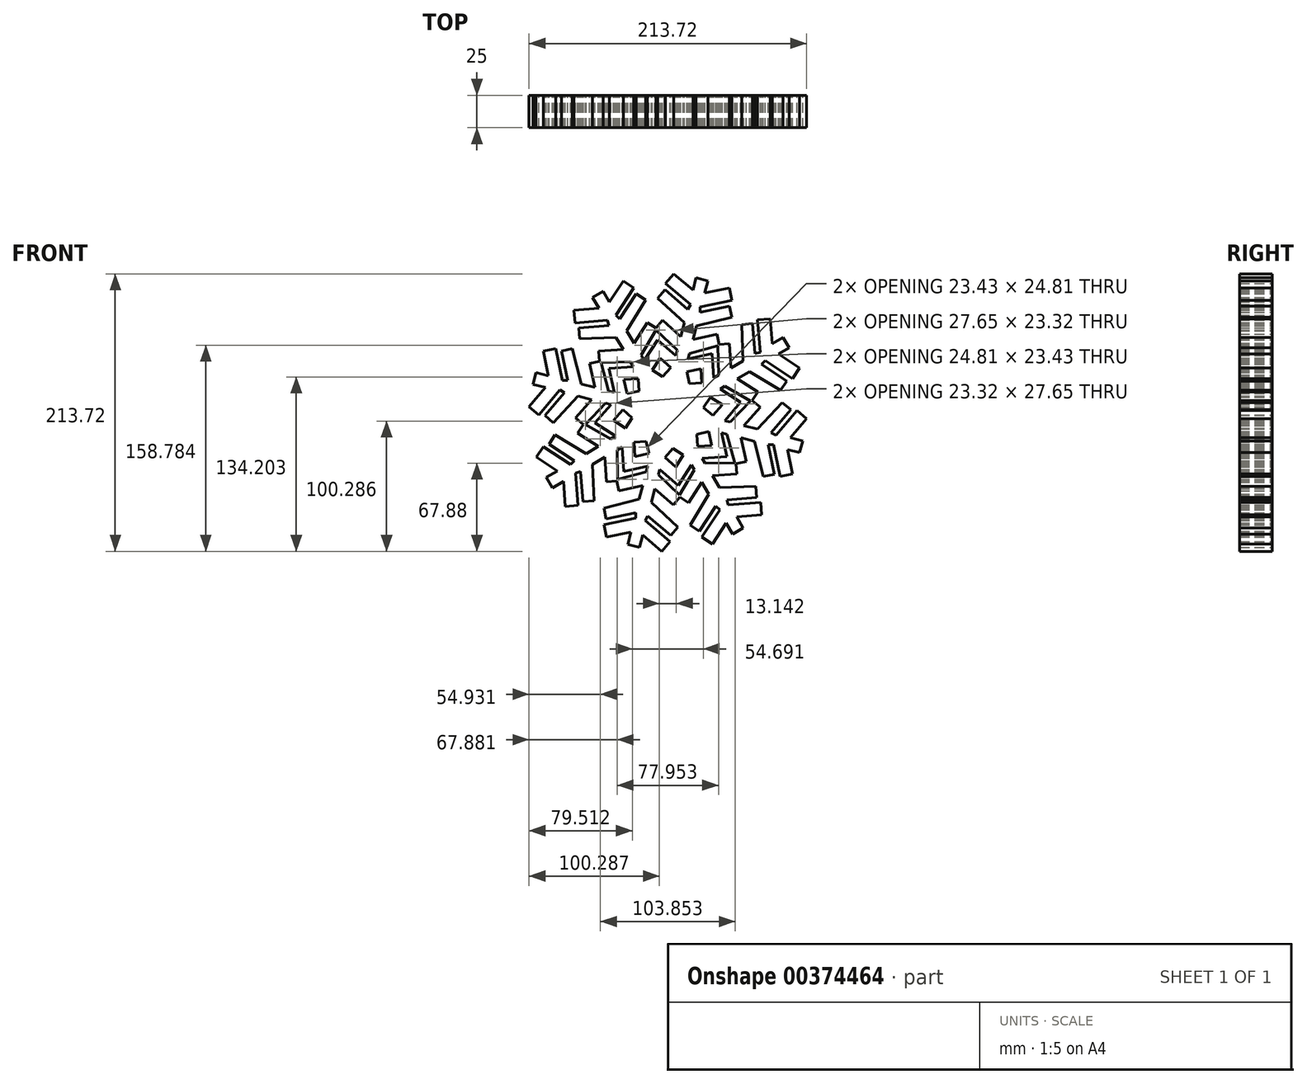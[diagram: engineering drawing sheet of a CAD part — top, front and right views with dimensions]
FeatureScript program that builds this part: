
annotation { "Feature Type Name" : "Feature", "Feature Type Description" : "" }
export const myFeature = defineFeature(function(context is Context, id is Id, definition is map)
    precondition{}
    {
        {
            var Q0;
            Q0=qCreatedBy(makeId("Front.planeOp"),FACE);
            var sketch = newSketch(context, id + "F0", { "sketchPlane" : qUnion([Q0])});
            skPoint(sketch, "E0.first.point", {"position": v(-46.74, 41.12) * mm});
            skPoint(sketch, "E0.second.point", {"position": v(0, 29.5) * mm});
            skPoint(sketch, "E0.third.point", {"position": v(-21.47, 0) * mm});
            skLineSegment(sketch, "E1", {"start": v(5.05, 127.1) * mm, "end": v(2.64, 117.71) * mm});
            skLineSegment(sketch, "E2", {"start": v(2.64, 117.71) * mm, "end": v(21.57, 121.6) * mm});
            skLineSegment(sketch, "E3", {"start": v(21.57, 121.6) * mm, "end": v(23.54, 112.02) * mm});
            skLineSegment(sketch, "E4", {"start": v(23.54, 112.02) * mm, "end": v(-1, 106.97) * mm});
            skLineSegment(sketch, "E5", {"start": v(-1, 106.97) * mm, "end": v(-1, 102.86) * mm});
            skLineSegment(sketch, "E6", {"start": v(-1, 102.86) * mm, "end": v(21.7, 107.53) * mm});
            skLineSegment(sketch, "E7", {"start": v(21.7, 107.53) * mm, "end": v(23.41, 99.23) * mm});
            skLineSegment(sketch, "E8", {"start": v(23.41, 99.23) * mm, "end": v(-3.7, 92.41) * mm});
            skLineSegment(sketch, "E9", {"start": v(-3.7, 92.41) * mm, "end": v(-6.38, 81.93) * mm});
            skLineSegment(sketch, "E10", {"start": v(-6.38, 81.93) * mm, "end": v(12.02, 86) * mm});
            skLineSegment(sketch, "E11", {"start": v(12.02, 86) * mm, "end": v(13.63, 78.2) * mm});
            skLineSegment(sketch, "E12", {"start": v(13.8, 77.34) * mm, "end": v(-9.05, 71.25) * mm});
            skLineSegment(sketch, "E13", {"start": v(-9.05, 71.25) * mm, "end": v(-10.13, 67) * mm});
            skLineSegment(sketch, "E14", {"start": v(-10.13, 67) * mm, "end": v(8.24, 71.01) * mm});
            skLineSegment(sketch, "E15", {"start": v(-0.39, 59.51) * mm, "end": v(-11.08, 57.14) * mm});
            skLineSegment(sketch, "E16", {"start": v(-11.08, 57.14) * mm, "end": v(-9.05, 47.8) * mm});
            skLineSegment(sketch, "E17", {"start": v(0.52, 128.27) * mm, "end": v(5.05, 127.1) * mm});
            skPoint(sketch, "E18.orphan", {"position": v(0, 107.18) * mm});
            skLineSegment(sketch, "E19.MirrorCS", {"start": v(-23.5, 60.32) * mm, "end": v(-29.78, 53.12) * mm});
            skLineSegment(sketch, "E20.MirrorCS", {"start": v(-31.74, 67.55) * mm, "end": v(-23.5, 60.32) * mm});
            skLineSegment(sketch, "E21.MirrorCS", {"start": v(-19.6, 69.43) * mm, "end": v(-33.77, 81.78) * mm});
            skLineSegment(sketch, "E22.MirrorCS", {"start": v(-18.5, 73.67) * mm, "end": v(-19.6, 69.43) * mm});
            skLineSegment(sketch, "E23.MirrorCS", {"start": v(-35.6, 90) * mm, "end": v(-18.5, 73.67) * mm});
            skLineSegment(sketch, "E24.MirrorCS", {"start": v(-29.88, 96.74) * mm, "end": v(-35.04, 90.67) * mm});
            skLineSegment(sketch, "E25.MirrorCS", {"start": v(-15.7, 84.32) * mm, "end": v(-29.88, 96.74) * mm});
            skLineSegment(sketch, "E26.MirrorCS", {"start": v(-13.02, 94.8) * mm, "end": v(-15.7, 84.32) * mm});
            skLineSegment(sketch, "E27.MirrorCS", {"start": v(-33.5, 113.82) * mm, "end": v(-13.02, 94.8) * mm});
            skLineSegment(sketch, "E28.MirrorCS", {"start": v(-28.02, 120.27) * mm, "end": v(-33.5, 113.82) * mm});
            skLineSegment(sketch, "E29.MirrorCS", {"start": v(-10.37, 105.26) * mm, "end": v(-28.02, 120.27) * mm});
            skLineSegment(sketch, "E30.MirrorCS", {"start": v(-8.39, 108.87) * mm, "end": v(-10.37, 105.26) * mm});
            skLineSegment(sketch, "E31.MirrorCS", {"start": v(-27.47, 125.1) * mm, "end": v(-8.39, 108.87) * mm});
            skLineSegment(sketch, "E32.MirrorCS", {"start": v(-21.13, 132.55) * mm, "end": v(-27.47, 125.1) * mm});
            skLineSegment(sketch, "E33.MirrorCS", {"start": v(-6.41, 120.03) * mm, "end": v(-21.13, 132.55) * mm});
            skLineSegment(sketch, "E34.MirrorCS", {"start": v(0.52, 128.27) * mm, "end": v(-4, 129.43) * mm});
            skLineSegment(sketch, "E35.MirrorCS", {"start": v(-4, 129.43) * mm, "end": v(-6.41, 120.03) * mm});
            skLineSegment(sketch, "E36.1.0", {"start": v(-52.33, 60.98) * mm, "end": v(-71.09, 59.69) * mm});
            skPoint(sketch, "E36.1.1", {"position": v(-65.17, 101.53) * mm});
            skLineSegment(sketch, "E36.1.2", {"start": v(-71.14, 92.84) * mm, "end": v(-94.24, 90.97) * mm});
            skLineSegment(sketch, "E36.1.3", {"start": v(-34.31, 90.2) * mm, "end": v(-46.16, 69.73) * mm});
            skPoint(sketch, "E36.1.4", {"position": v(-4.56, 10.56) * mm});
            skPoint(sketch, "E36.1.5", {"position": v(-10.24, 46.6) * mm});
            skLineSegment(sketch, "E36.1.6", {"start": v(-62.82, 97.77) * mm, "end": v(-50.07, 117.12) * mm});
            skLineSegment(sketch, "E36.1.7", {"start": v(-51.95, 121.6) * mm, "end": v(-65.73, 100.68) * mm});
            skLineSegment(sketch, "E36.1.10", {"start": v(-51.82, 79.16) * mm, "end": v(-41.7, 95.06) * mm});
            skLineSegment(sketch, "E36.1.11", {"start": v(-43, 112.46) * mm, "end": v(-57.34, 88.47) * mm});
            skLineSegment(sketch, "E36.1.12", {"start": v(-93.56, 82.53) * mm, "end": v(-65.63, 83.57) * mm});
            skPoint(sketch, "E36.1.13", {"position": v(-51.5, 21.76) * mm});
            skLineSegment(sketch, "E36.1.14", {"start": v(-78.8, 106.08) * mm, "end": v(-98.05, 104.53) * mm});
            skLineSegment(sketch, "E36.1.15", {"start": v(-60.11, 74.25) * mm, "end": v(-78.92, 73.02) * mm});
            skLineSegment(sketch, "E36.1.16", {"start": v(-77.15, 64.23) * mm, "end": v(-54.56, 64.75) * mm});
            skLineSegment(sketch, "E36.1.17", {"start": v(-97.26, 94.77) * mm, "end": v(-72.3, 96.8) * mm});
            skLineSegment(sketch, "E36.1.18", {"start": v(-43.93, 65.95) * mm, "end": v(-33.77, 81.78) * mm});
            skLineSegment(sketch, "E36.1.19", {"start": v(-59.59, 51.06) * mm, "end": v(-48.66, 51.77) * mm});
            skLineSegment(sketch, "E36.1.20", {"start": v(-48.66, 51.77) * mm, "end": v(-48, 42.24) * mm});
            skLineSegment(sketch, "E36.1.21", {"start": v(-70.75, 110.84) * mm, "end": v(-60.12, 126.98) * mm});
            skLineSegment(sketch, "E36.1.22", {"start": v(-37.62, 58.3) * mm, "end": v(-29.58, 53.14) * mm});
            skLineSegment(sketch, "E36.1.23", {"start": v(-31.74, 67.55) * mm, "end": v(-37.62, 58.3) * mm});
            skLineSegment(sketch, "E36.1.24", {"start": v(-72.3, 96.8) * mm, "end": v(-71.14, 92.84) * mm});
            skLineSegment(sketch, "E36.1.25", {"start": v(-46.16, 69.73) * mm, "end": v(-43.93, 65.95) * mm});
            skLineSegment(sketch, "E36.1.26", {"start": v(-94.24, 90.97) * mm, "end": v(-93.56, 82.53) * mm});
            skLineSegment(sketch, "E36.1.27", {"start": v(-41.7, 95.06) * mm, "end": v(-35.04, 90.67) * mm});
            skLineSegment(sketch, "E36.1.28", {"start": v(-83.73, 114.43) * mm, "end": v(-78.8, 106.08) * mm});
            skLineSegment(sketch, "E36.1.29", {"start": v(-50.07, 117.12) * mm, "end": v(-43, 112.46) * mm});
            skLineSegment(sketch, "E36.1.30", {"start": v(-60.12, 126.98) * mm, "end": v(-51.95, 121.6) * mm});
            skLineSegment(sketch, "E36.1.31", {"start": v(-75.7, 119.19) * mm, "end": v(-70.75, 110.84) * mm});
            skLineSegment(sketch, "E36.1.32", {"start": v(-57.34, 88.47) * mm, "end": v(-51.82, 79.16) * mm});
            skLineSegment(sketch, "E36.1.33", {"start": v(-65.63, 83.57) * mm, "end": v(-60.11, 74.25) * mm});
            skLineSegment(sketch, "E36.1.34", {"start": v(-78.92, 73.02) * mm, "end": v(-78.28, 65.08) * mm});
            skLineSegment(sketch, "E36.1.35", {"start": v(-98.05, 104.53) * mm, "end": v(-97.26, 94.77) * mm});
            skLineSegment(sketch, "E36.1.36", {"start": v(-54.56, 64.75) * mm, "end": v(-52.33, 60.98) * mm});
            skLineSegment(sketch, "E36.1.37", {"start": v(-65.73, 100.68) * mm, "end": v(-62.82, 97.77) * mm});
            skLineSegment(sketch, "E36.1.38", {"start": v(-79.71, 116.8) * mm, "end": v(-83.73, 114.43) * mm});
            skLineSegment(sketch, "E36.1.39", {"start": v(-79.71, 116.8) * mm, "end": v(-75.7, 119.19) * mm});
            skLineSegment(sketch, "E36.2.0", {"start": v(-69.5, 31.85) * mm, "end": v(-81.85, 17.68) * mm});
            skPoint(sketch, "E36.2.1", {"position": v(-107.25, 51.45) * mm});
            skLineSegment(sketch, "E36.2.2", {"start": v(-105.33, 41.08) * mm, "end": v(-120.35, 23.43) * mm});
            skLineSegment(sketch, "E36.2.3", {"start": v(-77.15, 64.23) * mm, "end": v(-71.33, 42.4) * mm});
            skPoint(sketch, "E36.2.4", {"position": v(-0.08, 29.98) * mm});
            skPoint(sketch, "E36.2.5", {"position": v(-29.58, 51.45) * mm});
            skLineSegment(sketch, "E36.2.6", {"start": v(-102.93, 50.45) * mm, "end": v(-107.6, 73.16) * mm});
            skLineSegment(sketch, "E36.2.7", {"start": v(-112.1, 74.99) * mm, "end": v(-107.05, 50.45) * mm});
            skLineSegment(sketch, "E36.2.10", {"start": v(-82, 45.07) * mm, "end": v(-86.08, 63.47) * mm});
            skLineSegment(sketch, "E36.2.11", {"start": v(-99.3, 74.86) * mm, "end": v(-92.49, 47.76) * mm});
            skLineSegment(sketch, "E36.2.12", {"start": v(-113.9, 17.94) * mm, "end": v(-94.88, 38.43) * mm});
            skPoint(sketch, "E36.2.13", {"position": v(-41.2, 4.7) * mm});
            skLineSegment(sketch, "E36.2.14", {"start": v(-120.1, 45.04) * mm, "end": v(-132.62, 30.32) * mm});
            skLineSegment(sketch, "E36.2.15", {"start": v(-84.4, 35.74) * mm, "end": v(-96.82, 21.57) * mm});
            skLineSegment(sketch, "E36.2.16", {"start": v(-90.08, 15.84) * mm, "end": v(-73.75, 32.94) * mm});
            skLineSegment(sketch, "E36.2.17", {"start": v(-125.17, 23.98) * mm, "end": v(-108.94, 43.06) * mm});
            skLineSegment(sketch, "E36.2.18", {"start": v(-67.08, 41.32) * mm, "end": v(-71.09, 59.69) * mm});
            skLineSegment(sketch, "E36.2.19", {"start": v(-67.62, 19.7) * mm, "end": v(-60.4, 27.94) * mm});
            skLineSegment(sketch, "E36.2.20", {"start": v(-60.4, 27.94) * mm, "end": v(-53.2, 21.67) * mm});
            skLineSegment(sketch, "E36.2.21", {"start": v(-117.79, 54.1) * mm, "end": v(-121.68, 73.02) * mm});
            skLineSegment(sketch, "E36.2.22", {"start": v(-57.22, 40.36) * mm, "end": v(-47.88, 42.4) * mm});
            skLineSegment(sketch, "E36.2.23", {"start": v(-59.59, 51.06) * mm, "end": v(-57.22, 40.36) * mm});
            skLineSegment(sketch, "E36.2.24", {"start": v(-108.94, 43.06) * mm, "end": v(-105.33, 41.08) * mm});
            skLineSegment(sketch, "E36.2.25", {"start": v(-71.33, 42.4) * mm, "end": v(-67.08, 41.32) * mm});
            skLineSegment(sketch, "E36.2.26", {"start": v(-120.35, 23.43) * mm, "end": v(-113.9, 17.94) * mm});
            skLineSegment(sketch, "E36.2.27", {"start": v(-86.08, 63.47) * mm, "end": v(-78.28, 65.08) * mm});
            skLineSegment(sketch, "E36.2.28", {"start": v(-129.5, 47.45) * mm, "end": v(-120.1, 45.04) * mm});
            skLineSegment(sketch, "E36.2.29", {"start": v(-107.6, 73.16) * mm, "end": v(-99.3, 74.86) * mm});
            skLineSegment(sketch, "E36.2.30", {"start": v(-121.68, 73.02) * mm, "end": v(-112.1, 74.99) * mm});
            skLineSegment(sketch, "E36.2.31", {"start": v(-127.18, 56.5) * mm, "end": v(-117.79, 54.1) * mm});
            skLineSegment(sketch, "E36.2.32", {"start": v(-92.49, 47.76) * mm, "end": v(-82, 45.07) * mm});
            skLineSegment(sketch, "E36.2.33", {"start": v(-94.88, 38.43) * mm, "end": v(-84.4, 35.74) * mm});
            skLineSegment(sketch, "E36.2.34", {"start": v(-96.82, 21.57) * mm, "end": v(-90.75, 16.4) * mm});
            skLineSegment(sketch, "E36.2.35", {"start": v(-132.62, 30.32) * mm, "end": v(-125.17, 23.98) * mm});
            skLineSegment(sketch, "E36.2.36", {"start": v(-73.75, 32.94) * mm, "end": v(-69.5, 31.85) * mm});
            skLineSegment(sketch, "E36.2.37", {"start": v(-107.05, 50.45) * mm, "end": v(-102.93, 50.45) * mm});
            skLineSegment(sketch, "E36.2.38", {"start": v(-128.34, 51.97) * mm, "end": v(-129.5, 47.45) * mm});
            skLineSegment(sketch, "E36.2.39", {"start": v(-128.34, 51.97) * mm, "end": v(-127.18, 56.5) * mm});
            skLineSegment(sketch, "E36.3.0", {"start": v(-61.05, -0.88) * mm, "end": v(-59.76, -19.64) * mm});
            skPoint(sketch, "E36.3.1", {"position": v(-101.6, -13.72) * mm});
            skLineSegment(sketch, "E36.3.2", {"start": v(-92.91, -19.7) * mm, "end": v(-91.04, -42.8) * mm});
            skLineSegment(sketch, "E36.3.3", {"start": v(-90.27, 17.14) * mm, "end": v(-69.8, 5.29) * mm});
            skPoint(sketch, "E36.3.4", {"position": v(-10.64, 46.89) * mm});
            skPoint(sketch, "E36.3.5", {"position": v(-46.68, 41.2) * mm});
            skLineSegment(sketch, "E36.3.6", {"start": v(-97.84, -11.37) * mm, "end": v(-117.2, 1.38) * mm});
            skLineSegment(sketch, "E36.3.7", {"start": v(-121.67, -0.5) * mm, "end": v(-100.75, -14.28) * mm});
            skLineSegment(sketch, "E36.3.10", {"start": v(-79.23, -0.38) * mm, "end": v(-95.13, 9.75) * mm});
            skLineSegment(sketch, "E36.3.11", {"start": v(-112.54, 8.46) * mm, "end": v(-88.55, -5.89) * mm});
            skLineSegment(sketch, "E36.3.12", {"start": v(-82.6, -42.1) * mm, "end": v(-83.64, -14.18) * mm});
            skPoint(sketch, "E36.3.13", {"position": v(-21.84, -0.06) * mm});
            skLineSegment(sketch, "E36.3.14", {"start": v(-106.16, -27.34) * mm, "end": v(-104.6, -46.6) * mm});
            skLineSegment(sketch, "E36.3.15", {"start": v(-74.33, -8.66) * mm, "end": v(-73.1, -27.47) * mm});
            skLineSegment(sketch, "E36.3.16", {"start": v(-64.28, -26.76) * mm, "end": v(-64.83, -3.12) * mm});
            skLineSegment(sketch, "E36.3.17", {"start": v(-94.84, -45.8) * mm, "end": v(-96.87, -20.84) * mm});
            skLineSegment(sketch, "E36.3.18", {"start": v(-66.03, 7.52) * mm, "end": v(-81.85, 17.68) * mm});
            skLineSegment(sketch, "E36.3.19", {"start": v(-51.13, -8.14) * mm, "end": v(-51.85, 2.8) * mm});
            skLineSegment(sketch, "E36.3.20", {"start": v(-51.85, 2.8) * mm, "end": v(-42.31, 3.45) * mm});
            skLineSegment(sketch, "E36.3.21", {"start": v(-110.92, -19.3) * mm, "end": v(-127.05, -8.67) * mm});
            skLineSegment(sketch, "E36.3.22", {"start": v(-58.38, 13.82) * mm, "end": v(-53.22, 21.87) * mm});
            skLineSegment(sketch, "E36.3.23", {"start": v(-67.62, 19.7) * mm, "end": v(-58.38, 13.82) * mm});
            skLineSegment(sketch, "E36.3.24", {"start": v(-96.87, -20.84) * mm, "end": v(-92.91, -19.7) * mm});
            skLineSegment(sketch, "E36.3.25", {"start": v(-69.8, 5.29) * mm, "end": v(-66.03, 7.52) * mm});
            skLineSegment(sketch, "E36.3.26", {"start": v(-91.04, -42.8) * mm, "end": v(-82.6, -42.1) * mm});
            skLineSegment(sketch, "E36.3.27", {"start": v(-95.13, 9.75) * mm, "end": v(-90.75, 16.4) * mm});
            skLineSegment(sketch, "E36.3.28", {"start": v(-114.5, -32.28) * mm, "end": v(-106.16, -27.34) * mm});
            skLineSegment(sketch, "E36.3.29", {"start": v(-117.2, 1.38) * mm, "end": v(-112.54, 8.46) * mm});
            skLineSegment(sketch, "E36.3.30", {"start": v(-127.05, -8.67) * mm, "end": v(-121.67, -0.5) * mm});
            skLineSegment(sketch, "E36.3.31", {"start": v(-119.27, -24.24) * mm, "end": v(-110.92, -19.3) * mm});
            skLineSegment(sketch, "E36.3.32", {"start": v(-88.55, -5.89) * mm, "end": v(-79.23, -0.38) * mm});
            skLineSegment(sketch, "E36.3.33", {"start": v(-83.64, -14.18) * mm, "end": v(-74.33, -8.66) * mm});
            skLineSegment(sketch, "E36.3.34", {"start": v(-73.1, -27.47) * mm, "end": v(-65.15, -26.83) * mm});
            skLineSegment(sketch, "E36.3.35", {"start": v(-104.6, -46.6) * mm, "end": v(-94.84, -45.8) * mm});
            skLineSegment(sketch, "E36.3.36", {"start": v(-64.83, -3.12) * mm, "end": v(-61.05, -0.88) * mm});
            skLineSegment(sketch, "E36.3.37", {"start": v(-100.75, -14.28) * mm, "end": v(-97.84, -11.37) * mm});
            skLineSegment(sketch, "E36.3.38", {"start": v(-116.88, -28.26) * mm, "end": v(-114.5, -32.28) * mm});
            skLineSegment(sketch, "E36.3.39", {"start": v(-116.88, -28.26) * mm, "end": v(-119.27, -24.24) * mm});
            skLineSegment(sketch, "E36.4.0", {"start": v(-31.93, -18.06) * mm, "end": v(-17.75, -30.4) * mm});
            skPoint(sketch, "E36.4.1", {"position": v(-51.52, -55.8) * mm});
            skLineSegment(sketch, "E36.4.2", {"start": v(-41.16, -53.88) * mm, "end": v(-23.5, -68.9) * mm});
            skLineSegment(sketch, "E36.4.3", {"start": v(-65.33, -25.97) * mm, "end": v(-42.48, -19.88) * mm});
            skPoint(sketch, "E36.4.4", {"position": v(-30.06, 51.37) * mm});
            skPoint(sketch, "E36.4.5", {"position": v(-51.52, 21.87) * mm});
            skLineSegment(sketch, "E36.4.6", {"start": v(-50.53, -51.48) * mm, "end": v(-73.23, -56.15) * mm});
            skLineSegment(sketch, "E36.4.7", {"start": v(-75.06, -60.65) * mm, "end": v(-50.53, -55.6) * mm});
            skLineSegment(sketch, "E36.4.10", {"start": v(-45.14, -30.55) * mm, "end": v(-63.54, -34.63) * mm});
            skLineSegment(sketch, "E36.4.11", {"start": v(-74.94, -47.86) * mm, "end": v(-47.83, -41.04) * mm});
            skLineSegment(sketch, "E36.4.12", {"start": v(-18.02, -62.44) * mm, "end": v(-38.5, -43.43) * mm});
            skPoint(sketch, "E36.4.13", {"position": v(-4.78, 10.26) * mm});
            skLineSegment(sketch, "E36.4.14", {"start": v(-45.11, -68.66) * mm, "end": v(-30.4, -81.17) * mm});
            skLineSegment(sketch, "E36.4.15", {"start": v(-35.82, -32.94) * mm, "end": v(-21.65, -45.37) * mm});
            skLineSegment(sketch, "E36.4.16", {"start": v(-15.92, -38.63) * mm, "end": v(-33.02, -22.3) * mm});
            skLineSegment(sketch, "E36.4.17", {"start": v(-24.06, -73.72) * mm, "end": v(-43.14, -57.5) * mm});
            skLineSegment(sketch, "E36.4.18", {"start": v(-41.4, -15.63) * mm, "end": v(-59.76, -19.64) * mm});
            skLineSegment(sketch, "E36.4.19", {"start": v(-19.78, -16.17) * mm, "end": v(-28.02, -8.95) * mm});
            skLineSegment(sketch, "E36.4.20", {"start": v(-28.02, -8.95) * mm, "end": v(-21.74, -1.74) * mm});
            skLineSegment(sketch, "E36.4.21", {"start": v(-54.17, -66.34) * mm, "end": v(-73.1, -70.23) * mm});
            skLineSegment(sketch, "E36.4.22", {"start": v(-40.44, -5.77) * mm, "end": v(-42.48, 3.57) * mm});
            skLineSegment(sketch, "E36.4.23", {"start": v(-51.13, -8.14) * mm, "end": v(-40.44, -5.77) * mm});
            skLineSegment(sketch, "E36.4.24", {"start": v(-43.14, -57.5) * mm, "end": v(-41.16, -53.88) * mm});
            skLineSegment(sketch, "E36.4.25", {"start": v(-42.48, -19.88) * mm, "end": v(-41.4, -15.63) * mm});
            skLineSegment(sketch, "E36.4.26", {"start": v(-23.5, -68.9) * mm, "end": v(-18.02, -62.44) * mm});
            skLineSegment(sketch, "E36.4.27", {"start": v(-63.54, -34.63) * mm, "end": v(-65.15, -26.83) * mm});
            skLineSegment(sketch, "E36.4.28", {"start": v(-47.52, -78.05) * mm, "end": v(-45.11, -68.66) * mm});
            skLineSegment(sketch, "E36.4.29", {"start": v(-73.23, -56.15) * mm, "end": v(-74.94, -47.86) * mm});
            skLineSegment(sketch, "E36.4.30", {"start": v(-73.1, -70.23) * mm, "end": v(-75.06, -60.65) * mm});
            skLineSegment(sketch, "E36.4.31", {"start": v(-56.57, -75.73) * mm, "end": v(-54.17, -66.34) * mm});
            skLineSegment(sketch, "E36.4.32", {"start": v(-47.83, -41.04) * mm, "end": v(-45.14, -30.55) * mm});
            skLineSegment(sketch, "E36.4.33", {"start": v(-38.5, -43.43) * mm, "end": v(-35.82, -32.94) * mm});
            skLineSegment(sketch, "E36.4.34", {"start": v(-21.65, -45.37) * mm, "end": v(-16.48, -39.3) * mm});
            skLineSegment(sketch, "E36.4.35", {"start": v(-30.4, -81.17) * mm, "end": v(-24.06, -73.72) * mm});
            skLineSegment(sketch, "E36.4.36", {"start": v(-33.02, -22.3) * mm, "end": v(-31.93, -18.06) * mm});
            skLineSegment(sketch, "E36.4.37", {"start": v(-50.53, -55.6) * mm, "end": v(-50.53, -51.48) * mm});
            skLineSegment(sketch, "E36.4.38", {"start": v(-52.05, -76.9) * mm, "end": v(-47.52, -78.05) * mm});
            skLineSegment(sketch, "E36.4.39", {"start": v(-52.05, -76.9) * mm, "end": v(-56.57, -75.73) * mm});
            skLineSegment(sketch, "E36.5.0", {"start": v(0.8, -9.6) * mm, "end": v(19.57, -8.31) * mm});
            skPoint(sketch, "E36.5.1", {"position": v(13.64, -50.15) * mm});
            skLineSegment(sketch, "E36.5.2", {"start": v(19.61, -41.47) * mm, "end": v(42.72, -39.6) * mm});
            skLineSegment(sketch, "E36.5.3", {"start": v(-17.21, -38.82) * mm, "end": v(-5.36, -18.35) * mm});
            skPoint(sketch, "E36.5.4", {"position": v(-46.96, 40.81) * mm});
            skPoint(sketch, "E36.5.5", {"position": v(-41.28, 4.77) * mm});
            skLineSegment(sketch, "E36.5.6", {"start": v(11.3, -46.4) * mm, "end": v(-1.46, -65.75) * mm});
            skLineSegment(sketch, "E36.5.7", {"start": v(0.42, -70.22) * mm, "end": v(14.2, -49.3) * mm});
            skLineSegment(sketch, "E36.5.10", {"start": v(0.3, -27.78) * mm, "end": v(-9.82, -43.68) * mm});
            skLineSegment(sketch, "E36.5.11", {"start": v(-8.53, -61.09) * mm, "end": v(5.81, -37.1) * mm});
            skLineSegment(sketch, "E36.5.12", {"start": v(42.03, -31.15) * mm, "end": v(14.1, -32.2) * mm});
            skPoint(sketch, "E36.5.13", {"position": v(-0.02, 29.61) * mm});
            skLineSegment(sketch, "E36.5.14", {"start": v(27.27, -54.71) * mm, "end": v(46.52, -53.15) * mm});
            skLineSegment(sketch, "E36.5.15", {"start": v(8.59, -22.88) * mm, "end": v(27.4, -21.65) * mm});
            skLineSegment(sketch, "E36.5.16", {"start": v(26.68, -12.83) * mm, "end": v(3.04, -13.38) * mm});
            skLineSegment(sketch, "E36.5.17", {"start": v(45.73, -43.4) * mm, "end": v(20.77, -45.42) * mm});
            skLineSegment(sketch, "E36.5.18", {"start": v(-7.6, -14.58) * mm, "end": v(-17.75, -30.4) * mm});
            skLineSegment(sketch, "E36.5.19", {"start": v(8.06, 0.31) * mm, "end": v(-2.87, -0.4) * mm});
            skLineSegment(sketch, "E36.5.20", {"start": v(-2.87, -0.4) * mm, "end": v(-3.52, 9.14) * mm});
            skLineSegment(sketch, "E36.5.21", {"start": v(19.23, -59.47) * mm, "end": v(8.6, -75.6) * mm});
            skLineSegment(sketch, "E36.5.22", {"start": v(-13.9, -6.93) * mm, "end": v(-21.95, -1.77) * mm});
            skLineSegment(sketch, "E36.5.23", {"start": v(-19.78, -16.17) * mm, "end": v(-13.9, -6.93) * mm});
            skLineSegment(sketch, "E36.5.24", {"start": v(20.77, -45.42) * mm, "end": v(19.61, -41.47) * mm});
            skLineSegment(sketch, "E36.5.25", {"start": v(-5.36, -18.35) * mm, "end": v(-7.6, -14.58) * mm});
            skLineSegment(sketch, "E36.5.26", {"start": v(42.72, -39.6) * mm, "end": v(42.03, -31.15) * mm});
            skLineSegment(sketch, "E36.5.27", {"start": v(-9.82, -43.68) * mm, "end": v(-16.48, -39.3) * mm});
            skLineSegment(sketch, "E36.5.28", {"start": v(32.2, -63.06) * mm, "end": v(27.27, -54.71) * mm});
            skLineSegment(sketch, "E36.5.29", {"start": v(-1.46, -65.75) * mm, "end": v(-8.53, -61.09) * mm});
            skLineSegment(sketch, "E36.5.30", {"start": v(8.6, -75.6) * mm, "end": v(0.42, -70.22) * mm});
            skLineSegment(sketch, "E36.5.31", {"start": v(24.17, -67.82) * mm, "end": v(19.23, -59.47) * mm});
            skLineSegment(sketch, "E36.5.32", {"start": v(5.81, -37.1) * mm, "end": v(0.3, -27.78) * mm});
            skLineSegment(sketch, "E36.5.33", {"start": v(14.1, -32.2) * mm, "end": v(8.59, -22.88) * mm});
            skLineSegment(sketch, "E36.5.34", {"start": v(27.4, -21.65) * mm, "end": v(26.75, -13.7) * mm});
            skLineSegment(sketch, "E36.5.35", {"start": v(46.52, -53.15) * mm, "end": v(45.73, -43.4) * mm});
            skLineSegment(sketch, "E36.5.36", {"start": v(3.04, -13.38) * mm, "end": v(0.8, -9.6) * mm});
            skLineSegment(sketch, "E36.5.37", {"start": v(14.2, -49.3) * mm, "end": v(11.3, -46.4) * mm});
            skLineSegment(sketch, "E36.5.38", {"start": v(28.19, -65.44) * mm, "end": v(32.2, -63.06) * mm});
            skLineSegment(sketch, "E36.5.39", {"start": v(28.19, -65.44) * mm, "end": v(24.17, -67.82) * mm});
            skLineSegment(sketch, "E36.6.0", {"start": v(17.98, 19.52) * mm, "end": v(30.33, 33.7) * mm});
            skPoint(sketch, "E36.6.1", {"position": v(55.73, -0.08) * mm});
            skLineSegment(sketch, "E36.6.2", {"start": v(53.8, 10.29) * mm, "end": v(68.82, 27.95) * mm});
            skLineSegment(sketch, "E36.6.3", {"start": v(25.9, -13.88) * mm, "end": v(19.8, 8.97) * mm});
            skPoint(sketch, "E36.6.4", {"position": v(-51.45, 21.4) * mm});
            skPoint(sketch, "E36.6.5", {"position": v(-21.95, -0.08) * mm});
            skLineSegment(sketch, "E36.6.6", {"start": v(51.4, 0.92) * mm, "end": v(56.08, -21.78) * mm});
            skLineSegment(sketch, "E36.6.7", {"start": v(60.57, -23.61) * mm, "end": v(55.52, 0.92) * mm});
            skLineSegment(sketch, "E36.6.10", {"start": v(30.48, 6.3) * mm, "end": v(34.56, -12.1) * mm});
            skLineSegment(sketch, "E36.6.11", {"start": v(47.78, -23.49) * mm, "end": v(40.96, 3.62) * mm});
            skLineSegment(sketch, "E36.6.12", {"start": v(62.37, 33.43) * mm, "end": v(43.35, 12.95) * mm});
            skPoint(sketch, "E36.6.13", {"position": v(-10.33, 46.67) * mm});
            skLineSegment(sketch, "E36.6.14", {"start": v(68.58, 6.33) * mm, "end": v(81.1, 21.05) * mm});
            skLineSegment(sketch, "E36.6.15", {"start": v(32.87, 15.63) * mm, "end": v(45.3, 29.8) * mm});
            skLineSegment(sketch, "E36.6.16", {"start": v(38.56, 35.53) * mm, "end": v(22.23, 18.43) * mm});
            skLineSegment(sketch, "E36.6.17", {"start": v(73.64, 27.4) * mm, "end": v(57.42, 8.31) * mm});
            skLineSegment(sketch, "E36.6.18", {"start": v(15.56, 10.06) * mm, "end": v(19.57, -8.31) * mm});
            skLineSegment(sketch, "E36.6.19", {"start": v(16.1, 31.66) * mm, "end": v(8.87, 23.43) * mm});
            skLineSegment(sketch, "E36.6.20", {"start": v(8.87, 23.43) * mm, "end": v(1.67, 29.7) * mm});
            skLineSegment(sketch, "E36.6.21", {"start": v(66.26, -2.72) * mm, "end": v(70.16, -21.64) * mm});
            skLineSegment(sketch, "E36.6.22", {"start": v(5.7, 11) * mm, "end": v(-3.65, 8.97) * mm});
            skLineSegment(sketch, "E36.6.23", {"start": v(8.06, 0.31) * mm, "end": v(5.7, 11) * mm});
            skLineSegment(sketch, "E36.6.24", {"start": v(57.42, 8.31) * mm, "end": v(53.8, 10.29) * mm});
            skLineSegment(sketch, "E36.6.25", {"start": v(19.8, 8.97) * mm, "end": v(15.56, 10.06) * mm});
            skLineSegment(sketch, "E36.6.26", {"start": v(68.82, 27.95) * mm, "end": v(62.37, 33.43) * mm});
            skLineSegment(sketch, "E36.6.27", {"start": v(34.56, -12.1) * mm, "end": v(26.75, -13.7) * mm});
            skLineSegment(sketch, "E36.6.28", {"start": v(77.98, 3.93) * mm, "end": v(68.58, 6.33) * mm});
            skLineSegment(sketch, "E36.6.29", {"start": v(56.08, -21.78) * mm, "end": v(47.78, -23.49) * mm});
            skLineSegment(sketch, "E36.6.30", {"start": v(70.16, -21.64) * mm, "end": v(60.57, -23.61) * mm});
            skLineSegment(sketch, "E36.6.31", {"start": v(75.66, -5.13) * mm, "end": v(66.26, -2.72) * mm});
            skLineSegment(sketch, "E36.6.32", {"start": v(40.96, 3.62) * mm, "end": v(30.48, 6.3) * mm});
            skLineSegment(sketch, "E36.6.33", {"start": v(43.35, 12.95) * mm, "end": v(32.87, 15.63) * mm});
            skLineSegment(sketch, "E36.6.34", {"start": v(45.3, 29.8) * mm, "end": v(39.22, 34.97) * mm});
            skLineSegment(sketch, "E36.6.35", {"start": v(81.1, 21.05) * mm, "end": v(73.64, 27.4) * mm});
            skLineSegment(sketch, "E36.6.36", {"start": v(22.23, 18.43) * mm, "end": v(17.98, 19.52) * mm});
            skLineSegment(sketch, "E36.6.37", {"start": v(55.52, 0.92) * mm, "end": v(51.4, 0.92) * mm});
            skLineSegment(sketch, "E36.6.38", {"start": v(76.82, -0.6) * mm, "end": v(77.98, 3.93) * mm});
            skLineSegment(sketch, "E36.6.39", {"start": v(76.82, -0.6) * mm, "end": v(75.66, -5.13) * mm});
            skLineSegment(sketch, "E36.7.0", {"start": v(9.53, 52.26) * mm, "end": v(8.24, 71.01) * mm});
            skPoint(sketch, "E36.7.1", {"position": v(50.08, 65.1) * mm});
            skLineSegment(sketch, "E36.7.2", {"start": v(41.39, 71.06) * mm, "end": v(39.52, 94.17) * mm});
            skLineSegment(sketch, "E36.7.3", {"start": v(38.74, 34.24) * mm, "end": v(18.28, 46.08) * mm});
            skPoint(sketch, "E36.7.4", {"position": v(-40.89, 4.49) * mm});
            skPoint(sketch, "E36.7.5", {"position": v(-4.85, 10.17) * mm});
            skLineSegment(sketch, "E36.7.6", {"start": v(46.32, 62.74) * mm, "end": v(65.67, 50) * mm});
            skLineSegment(sketch, "E36.7.7", {"start": v(70.15, 51.87) * mm, "end": v(49.23, 65.65) * mm});
            skLineSegment(sketch, "E36.7.10", {"start": v(27.7, 51.75) * mm, "end": v(43.6, 41.62) * mm});
            skLineSegment(sketch, "E36.7.11", {"start": v(61.01, 42.92) * mm, "end": v(37.02, 57.26) * mm});
            skLineSegment(sketch, "E36.7.12", {"start": v(31.08, 93.48) * mm, "end": v(32.12, 65.55) * mm});
            skPoint(sketch, "E36.7.13", {"position": v(-29.69, 51.43) * mm});
            skLineSegment(sketch, "E36.7.14", {"start": v(54.63, 78.72) * mm, "end": v(53.08, 97.97) * mm});
            skLineSegment(sketch, "E36.7.15", {"start": v(22.8, 60.04) * mm, "end": v(21.57, 78.84) * mm});
            skLineSegment(sketch, "E36.7.16", {"start": v(12.75, 78.13) * mm, "end": v(13.3, 54.49) * mm});
            skLineSegment(sketch, "E36.7.17", {"start": v(43.32, 97.18) * mm, "end": v(45.34, 72.22) * mm});
            skLineSegment(sketch, "E36.7.18", {"start": v(14.5, 43.85) * mm, "end": v(30.33, 33.7) * mm});
            skLineSegment(sketch, "E36.7.19", {"start": v(-0.39, 59.51) * mm, "end": v(0.33, 48.58) * mm});
            skLineSegment(sketch, "E36.7.20", {"start": v(0.33, 48.58) * mm, "end": v(-9.21, 47.93) * mm});
            skLineSegment(sketch, "E36.7.21", {"start": v(59.4, 70.67) * mm, "end": v(75.53, 60.05) * mm});
            skLineSegment(sketch, "E36.7.22", {"start": v(6.86, 37.55) * mm, "end": v(1.7, 29.5) * mm});
            skLineSegment(sketch, "E36.7.23", {"start": v(16.1, 31.66) * mm, "end": v(6.86, 37.55) * mm});
            skLineSegment(sketch, "E36.7.24", {"start": v(45.34, 72.22) * mm, "end": v(41.39, 71.06) * mm});
            skLineSegment(sketch, "E36.7.25", {"start": v(18.28, 46.08) * mm, "end": v(14.5, 43.85) * mm});
            skLineSegment(sketch, "E36.7.26", {"start": v(39.52, 94.17) * mm, "end": v(31.08, 93.48) * mm});
            skLineSegment(sketch, "E36.7.27", {"start": v(43.6, 41.62) * mm, "end": v(39.22, 34.97) * mm});
            skLineSegment(sketch, "E36.7.28", {"start": v(62.98, 83.66) * mm, "end": v(54.63, 78.72) * mm});
            skLineSegment(sketch, "E36.7.29", {"start": v(65.67, 50) * mm, "end": v(61.01, 42.92) * mm});
            skLineSegment(sketch, "E36.7.30", {"start": v(75.53, 60.05) * mm, "end": v(70.15, 51.87) * mm});
            skLineSegment(sketch, "E36.7.31", {"start": v(67.74, 75.61) * mm, "end": v(59.4, 70.67) * mm});
            skLineSegment(sketch, "E36.7.32", {"start": v(37.02, 57.26) * mm, "end": v(27.7, 51.75) * mm});
            skLineSegment(sketch, "E36.7.33", {"start": v(32.12, 65.55) * mm, "end": v(22.8, 60.04) * mm});
            skLineSegment(sketch, "E36.7.34", {"start": v(21.57, 78.84) * mm, "end": v(13.63, 78.2) * mm});
            skLineSegment(sketch, "E36.7.35", {"start": v(53.08, 97.97) * mm, "end": v(43.32, 97.18) * mm});
            skLineSegment(sketch, "E36.7.36", {"start": v(13.3, 54.49) * mm, "end": v(9.53, 52.26) * mm});
            skLineSegment(sketch, "E36.7.37", {"start": v(49.23, 65.65) * mm, "end": v(46.32, 62.74) * mm});
            skLineSegment(sketch, "E36.7.38", {"start": v(65.36, 79.64) * mm, "end": v(62.98, 83.66) * mm});
            skLineSegment(sketch, "E36.7.39", {"start": v(65.36, 79.64) * mm, "end": v(67.74, 75.61) * mm});
            skPoint(sketch, "E36.center", {"position": v(-25.76, 25.69) * mm});
            skPoint(sketch, "E37.orphan", {"position": v(-78.2, 64.2) * mm});
            skPoint(sketch, "E38.orphan", {"position": v(-77.42, 65.25) * mm});
            skPoint(sketch, "E39.orphan", {"position": v(-70.92, 58.9) * mm});
            skPoint(sketch, "E40.orphan", {"position": v(-70.3, 59.74) * mm});
            skPoint(sketch, "E41.orphan", {"position": v(-59.45, 50.45) * mm});
            skPoint(sketch, "E42.orphan", {"position": v(-58.97, 51.1) * mm});
            skPoint(sketch, "E43.orphan", {"position": v(-34.2, 81.1) * mm});
            skPoint(sketch, "E44.orphan", {"position": v(-33.17, 81.25) * mm});
            skPoint(sketch, "E45.orphan", {"position": v(-32.07, 67.02) * mm});
            skPoint(sketch, "E46.orphan", {"position": v(-31.27, 67.14) * mm});
            skPoint(sketch, "E47.orphan", {"position": v(8.3, 70.22) * mm});
            skPoint(sketch, "E48.orphan", {"position": v(7.46, 70.84) * mm});
            skPoint(sketch, "E49.orphan", {"position": v(-1, 59.38) * mm});
            skPoint(sketch, "E50.orphan", {"position": v(-0.35, 58.9) * mm});
            skPoint(sketch, "E51.orphan", {"position": v(29.66, 34.13) * mm});
            skPoint(sketch, "E52.orphan", {"position": v(29.8, 33.1) * mm});
            skPoint(sketch, "E53.orphan", {"position": v(15.69, 31.2) * mm});
            skPoint(sketch, "E54.orphan", {"position": v(15.57, 32) * mm});
            skPoint(sketch, "E55.orphan", {"position": v(19.4, -7.53) * mm});
            skPoint(sketch, "E56.orphan", {"position": v(18.77, -8.37) * mm});
            skPoint(sketch, "E57.orphan", {"position": v(7.44, 0.27) * mm});
            skPoint(sketch, "E58.orphan", {"position": v(7.93, 0.92) * mm});
            skPoint(sketch, "E59.orphan", {"position": v(-20.25, -15.76) * mm});
            skPoint(sketch, "E60.orphan", {"position": v(-19.45, -15.65) * mm});
            skPoint(sketch, "E61.orphan", {"position": v(-18.35, -29.88) * mm});
            skPoint(sketch, "E62.orphan", {"position": v(-17.32, -29.73) * mm});
            skPoint(sketch, "E63.orphan", {"position": v(-59.82, -18.84) * mm});
            skPoint(sketch, "E64.orphan", {"position": v(-58.98, -19.47) * mm});
            skPoint(sketch, "E65.orphan", {"position": v(-51.18, -7.52) * mm});
            skPoint(sketch, "E66.orphan", {"position": v(-50.53, -8) * mm});
            skPoint(sketch, "E67.orphan", {"position": v(-81.33, 18.28) * mm});
            skPoint(sketch, "E68.orphan", {"position": v(-81.18, 17.24) * mm});
            skPoint(sketch, "E69.orphan", {"position": v(-67.21, 20.18) * mm});
            skPoint(sketch, "E70.orphan", {"position": v(-67.1, 19.38) * mm});
            skSolve(sketch);
        }
        {
            var Q0;
            Q0=makeQuery(id+"F0.imprint","IMPRINT",FACE,{"disambiguationData":[TD([[makeQuery(id+"F0.imprint","IMPRINT",EDGE,{"derivedFrom":sQuery(id+"F0.wireOp",EDGE,"E1")}),-1.0]])]});
            extrude(context, id + "F1", {"entities" : qUnion([Q0]), "depth" : 25 * mm});
        }
    });
